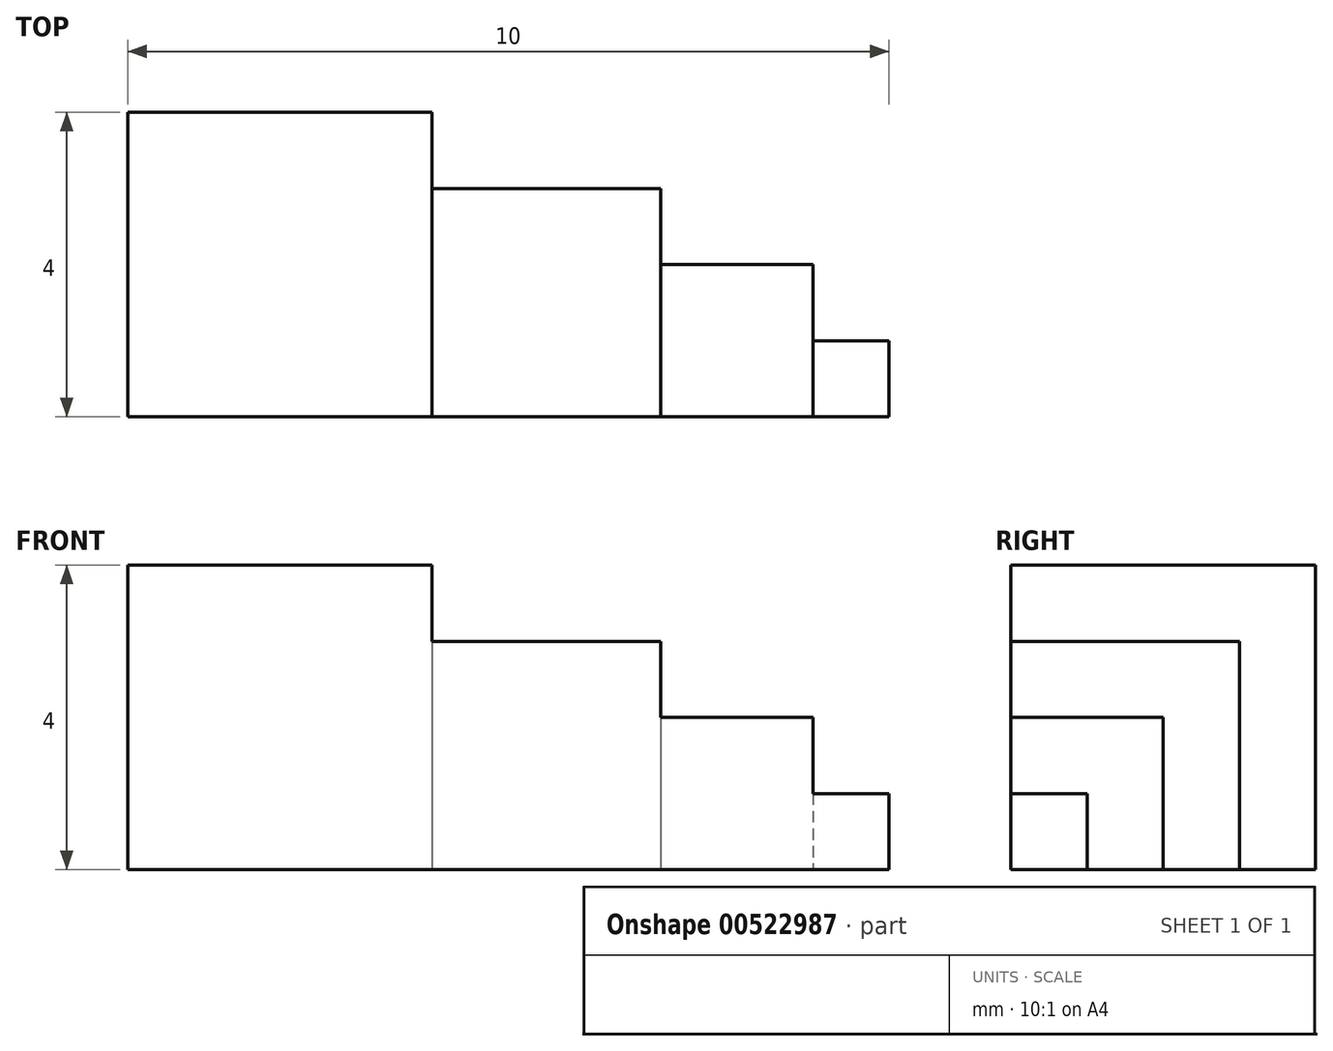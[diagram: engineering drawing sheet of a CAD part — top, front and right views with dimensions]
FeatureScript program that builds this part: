
annotation { "Feature Type Name" : "Feature", "Feature Type Description" : "" }
export const myFeature = defineFeature(function(context is Context, id is Id, definition is map)
    precondition{}
    {
        {
            var Q0;
            Q0=qCreatedBy(makeId("Top.planeOp"),FACE);
            var sketch = newSketch(context, id + "F0", { "sketchPlane" : qUnion([Q0])});
            skLineSegment(sketch, "E0.bottom", {"start": v(5, 0) * mm, "end": v(4, 0) * mm});
            skLineSegment(sketch, "E0.top", {"start": v(5, 1) * mm, "end": v(4, 1) * mm});
            skLineSegment(sketch, "E0.left", {"start": v(5, 0) * mm, "end": v(5, 1) * mm});
            skLineSegment(sketch, "E1", {"start": v(4, 1) * mm, "end": v(4, 2) * mm});
            skLineSegment(sketch, "E2", {"start": v(4, 2) * mm, "end": v(2, 2) * mm});
            skLineSegment(sketch, "E3", {"start": v(2, 2) * mm, "end": v(2, 3) * mm});
            skLineSegment(sketch, "E4", {"start": v(2, 3) * mm, "end": v(-1, 3) * mm});
            skLineSegment(sketch, "E5", {"start": v(-1, 3) * mm, "end": v(-1, 4) * mm});
            skLineSegment(sketch, "E6", {"start": v(-1, 4) * mm, "end": v(-5, 4) * mm});
            skLineSegment(sketch, "E7", {"start": v(4, 0) * mm, "end": v(-5, 0) * mm});
            skLineSegment(sketch, "E8", {"start": v(-5, 0) * mm, "end": v(-5, 4) * mm});
            skLineSegment(sketch, "E9.MirrorCS", {"start": v(-9, 4) * mm, "end": v(-5, 4) * mm});
            skLineSegment(sketch, "E10.MirrorCS", {"start": v(-9, 3) * mm, "end": v(-9, 4) * mm});
            skLineSegment(sketch, "E11.MirrorCS", {"start": v(-12, 3) * mm, "end": v(-9, 3) * mm});
            skLineSegment(sketch, "E12.MirrorCS", {"start": v(-12, 2) * mm, "end": v(-12, 3) * mm});
            skLineSegment(sketch, "E13.MirrorCS", {"start": v(-14, 2) * mm, "end": v(-12, 2) * mm});
            skLineSegment(sketch, "E14.MirrorCS", {"start": v(-14, 1) * mm, "end": v(-14, 2) * mm});
            skLineSegment(sketch, "E15.MirrorCS", {"start": v(-15, 1) * mm, "end": v(-14, 1) * mm});
            skLineSegment(sketch, "E16.MirrorCS", {"start": v(-15, 0) * mm, "end": v(-15, 1) * mm});
            skLineSegment(sketch, "E17.MirrorCS", {"start": v(-15, 0) * mm, "end": v(-14, 0) * mm});
            skLineSegment(sketch, "E18.MirrorCS", {"start": v(-14, 0) * mm, "end": v(-5, 0) * mm});
            skSolve(sketch);
        }
        {
            var Q0;
            Q0=makeQuery(id+"F0.imprint","IMPRINT",FACE,{"disambiguationData":[TD([[makeQuery(id+"F0.imprint","IMPRINT",EDGE,{"derivedFrom":sQuery(id+"F0.wireOp",EDGE,"E0.bottom")}),-1.0]])]});
            var Q1;
            Q1=makeQuery(id+"F0.imprint","IMPRINT",FACE,{"disambiguationData":[TD([[makeQuery(id+"F0.imprint","IMPRINT",EDGE,{"derivedFrom":sQuery(id+"F0.wireOp",EDGE,"E8")}),1.0]])]});
            extrude(context, id + "F1", {"entities" : qUnion([Q0, Q1]), "depth" : 4 * mm, "offsetDistance" : 25 * mm});
        }
        {
            var Q0;
            Q0=makeQuery(id+"F1.opExtrude","SWEPT_EDGE",EDGE,{"disambiguationData":[OSD([sQuery(id+"F0.wireOp",EDGE,"E9.MirrorCS"),sQuery(id+"F0.wireOp",EDGE,"E10.MirrorCS")])]});
            fillet(context, id + "F2", {"entities" : qUnion([Q0]), "radius" : 4 * mm, "tangentPropagation" : true, "allowEdgeOverflow" : false});
        }
        {
            var Q0;
            Q0=makeQuery(id+"F1.opExtrude","SWEPT_EDGE",EDGE,{"disambiguationData":[OSD([sQuery(id+"F0.wireOp",EDGE,"E11.MirrorCS"),sQuery(id+"F0.wireOp",EDGE,"E12.MirrorCS")])]});
            fillet(context, id + "F3", {"entities" : qUnion([Q0]), "radius" : 3 * mm, "tangentPropagation" : true, "allowEdgeOverflow" : false});
        }
        {
            var Q0;
            Q0=makeQuery(id+"F1.opExtrude","SWEPT_EDGE",EDGE,{"disambiguationData":[OSD([sQuery(id+"F0.wireOp",EDGE,"E13.MirrorCS"),sQuery(id+"F0.wireOp",EDGE,"E14.MirrorCS")])]});
            fillet(context, id + "F4", {"entities" : qUnion([Q0]), "radius" : 2 * mm, "tangentPropagation" : true, "allowEdgeOverflow" : false});
        }
        {
            var Q0;
            Q0=makeQuery(id+"F1.opExtrude","SWEPT_EDGE",EDGE,{"disambiguationData":[OSD([sQuery(id+"F0.wireOp",EDGE,"E15.MirrorCS"),sQuery(id+"F0.wireOp",EDGE,"E16.MirrorCS")])]});
            fillet(context, id + "F5", {"entities" : qUnion([Q0]), "radius" : 1 * mm, "tangentPropagation" : true, "allowEdgeOverflow" : false});
        }
        {
            var Q0;
            Q0=makeQuery(id+"F1.opExtrude","SWEPT_FACE",FACE,{"disambiguationData":[OSD([sQuery(id+"F0.wireOp",EDGE,"E0.bottom"),sQuery(id+"F0.wireOp",EDGE,"E7"),sQuery(id+"F0.wireOp",EDGE,"E17.MirrorCS"),sQuery(id+"F0.wireOp",EDGE,"E18.MirrorCS")])]});
            var sketch = newSketch(context, id + "F6", { "sketchPlane" : qUnion([Q0])});
            skLineSegment(sketch, "E19", {"start": v(5, 0) * mm, "end": v(5, 1) * mm});
            skLineSegment(sketch, "E20", {"start": v(5, 1) * mm, "end": v(4, 1) * mm});
            skLineSegment(sketch, "E21", {"start": v(4, 1) * mm, "end": v(4, 2) * mm});
            skLineSegment(sketch, "E22", {"start": v(4, 2) * mm, "end": v(2, 2) * mm});
            skLineSegment(sketch, "E23", {"start": v(2, 2) * mm, "end": v(2, 3) * mm});
            skLineSegment(sketch, "E24", {"start": v(2, 3) * mm, "end": v(-1, 3) * mm});
            skLineSegment(sketch, "E25", {"start": v(-1, 3) * mm, "end": v(-1, 4) * mm});
            skLineSegment(sketch, "E26", {"start": v(-1, 4) * mm, "end": v(-5, 4) * mm});
            skLineSegment(sketch, "E27", {"start": v(-5, 4) * mm, "end": v(-5, 0) * mm});
            skLineSegment(sketch, "E28", {"start": v(-5, 0) * mm, "end": v(5, 0) * mm});
            skSolve(sketch);
        }
        {
            var Q0;
            Q0 = qSketchRegion(id + "F6", true);
            extrude(context, id + "F7", {"entities" : qUnion([Q0]), "operationType" : NewBodyOperationType.INTERSECT, "oppositeDirection" : true, "depth" : 25 * mm, "offsetDistance" : 25 * mm});
        }
    });
